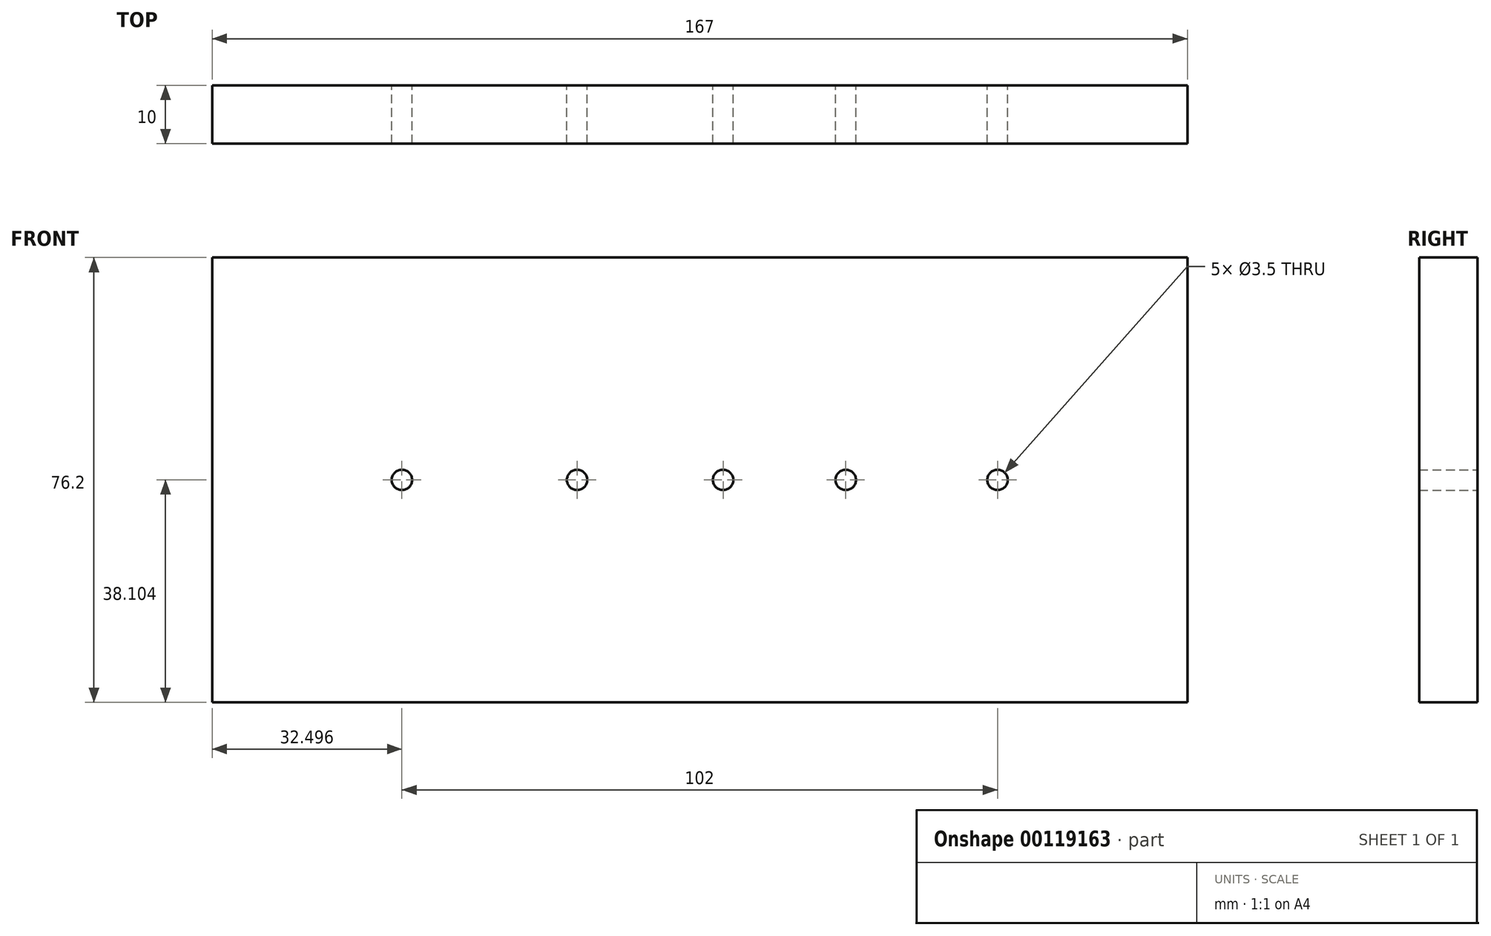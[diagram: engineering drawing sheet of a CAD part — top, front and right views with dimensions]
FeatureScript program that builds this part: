
annotation { "Feature Type Name" : "Feature", "Feature Type Description" : "" }
export const myFeature = defineFeature(function(context is Context, id is Id, definition is map)
    precondition{}
    {
        {
            var Q0;
            Q0=qCreatedBy(makeId("Front.planeOp"),FACE);
            var sketch = newSketch(context, id + "F0", { "sketchPlane" : qUnion([Q0])});
            skCircle(sketch, "E0", {"center": v(-38.31, 10.84) * mm, "radius": 1.75 * mm});
            skCircle(sketch, "E1.1.0.0", {"center": v(-8.31, 10.84) * mm, "radius": 1.75 * mm});
            skCircle(sketch, "E1.2.0.0", {"center": v(16.69, 10.84) * mm, "radius": 1.75 * mm});
            skCircle(sketch, "E1.3.0.0", {"center": v(37.69, 10.84) * mm, "radius": 1.75 * mm});
            skLineSegment(sketch, "E2", {"start": v(-38.31, 10.84) * mm, "end": v(-8.31, 10.84) * mm});
            skLineSegment(sketch, "E3", {"start": v(-8.31, 10.84) * mm, "end": v(16.69, 10.84) * mm});
            skLineSegment(sketch, "E4", {"start": v(37.69, 10.84) * mm, "end": v(16.69, 10.84) * mm});
            skLineSegment(sketch, "E5", {"start": v(37.69, 10.84) * mm, "end": v(63.69, 10.84) * mm});
            skCircle(sketch, "E6", {"center": v(63.69, 10.84) * mm, "radius": 1.75 * mm});
            skLineSegment(sketch, "E7", {"start": v(76.19, 48.94) * mm, "end": v(96.19, 48.94) * mm});
            skLineSegment(sketch, "E8", {"start": v(63.69, 10.84) * mm, "end": v(76.19, 10.84) * mm});
            skLineSegment(sketch, "E9", {"start": v(-70.81, 10.84) * mm, "end": v(-70.81, -27.26) * mm});
            skLineSegment(sketch, "E10", {"start": v(-62.1, -27.26) * mm, "end": v(-70.81, -27.26) * mm});
            skLineSegment(sketch, "E11.bottom", {"start": v(-70.81, -27.26) * mm, "end": v(96.19, -27.26) * mm});
            skLineSegment(sketch, "E11.top", {"start": v(-70.81, 48.94) * mm, "end": v(96.19, 48.94) * mm});
            skLineSegment(sketch, "E11.left", {"start": v(-70.81, -27.26) * mm, "end": v(-70.81, 48.94) * mm});
            skLineSegment(sketch, "E11.right", {"start": v(96.19, -27.26) * mm, "end": v(96.19, 48.94) * mm});
            skSolve(sketch);
        }
        {
            var Q0;
            Q0=makeQuery(id+"F0.imprint","IMPRINT",FACE,{"disambiguationData":[TD([[makeQuery(id+"F0.imprint","IMPRINT",EDGE,{"derivedFrom":sQuery(id+"F0.wireOp",EDGE,"E0")}),-1.0]])]});
            extrude(context, id + "F1", {"entities" : qUnion([Q0]), "depth" : 10 * mm});
        }
    });
